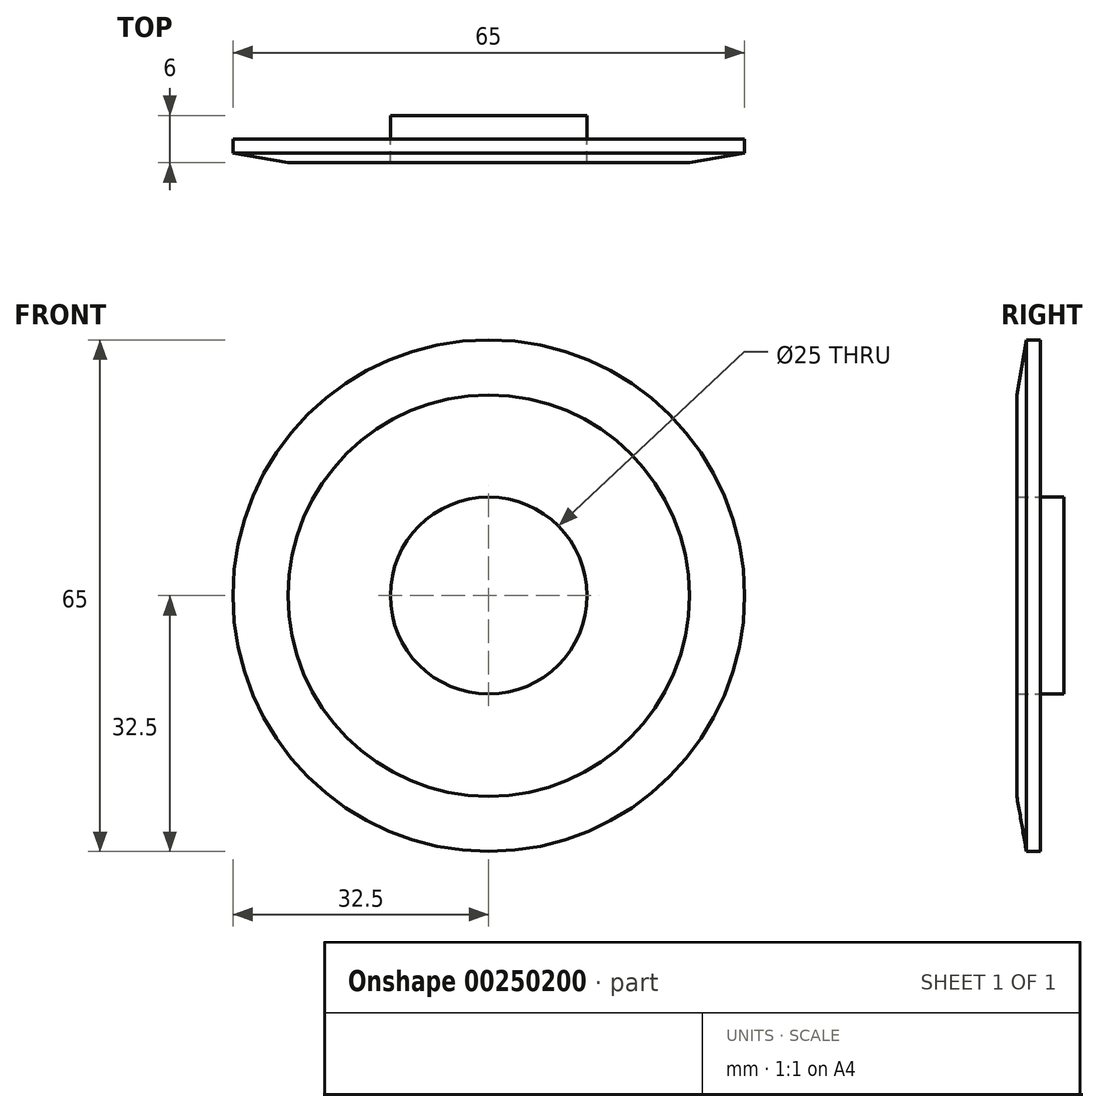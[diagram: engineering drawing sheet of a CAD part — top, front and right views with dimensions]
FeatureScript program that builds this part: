
annotation { "Feature Type Name" : "Feature", "Feature Type Description" : "" }
export const myFeature = defineFeature(function(context is Context, id is Id, definition is map)
    precondition{}
    {
        {
            var Q0;
            Q0=qCreatedBy(makeId("Front.planeOp"),FACE);
            var sketch = newSketch(context, id + "F0", { "sketchPlane" : qUnion([Q0])});
            skCircle(sketch, "E0", {"center": v(0, 0) * mm, "radius": 32.5 * mm});
            skCircle(sketch, "E1", {"center": v(0, 0) * mm, "radius": 12.5 * mm});
            skSolve(sketch);
        }
        {
            var Q0;
            Q0=makeQuery(id+"F0.imprint","IMPRINT",FACE,{"disambiguationData":[TD([[makeQuery(id+"F0.imprint","IMPRINT",EDGE,{"derivedFrom":sQuery(id+"F0.wireOp",EDGE,"E1")}),1.0]])]});
            extrude(context, id + "F1", {"entities" : qUnion([Q0]), "oppositeDirection" : true, "depth" : 3 * mm});
        }
        {
            var Q0;
            Q0 = qSketchRegion(id + "F0", true);
            extrude(context, id + "F2", {"entities" : qUnion([Q0]), "depth" : 3 * mm});
        }
        {
            var Q0;
            Q0=makeQuery(id+"F1.opExtrude","CAP_FACE",FACE,{"disambiguationData":[OSD([sQuery(id+"F0.wireOp",EDGE,"E1")])],"isStart":true});
            extrude(context, id + "F3", {"entities" : qUnion([Q0]), "depth" : 3 * mm});
        }
        {
            var Q0;
            Q0=makeQuery(id+"F2.opExtrude","CAP_EDGE",EDGE,{"disambiguationData":[OSD([sQuery(id+"F0.wireOp",EDGE,"E0")])],"isStart":false});
            chamfer(context, id + "F4", {"entities" : qUnion([Q0]), "chamferType" : ChamferType.OFFSET_ANGLE, "width" : 7 * mm, "oppositeDirection" : false, "angle" : 10 * degree, "tangentPropagation" : true});
        }
    });
